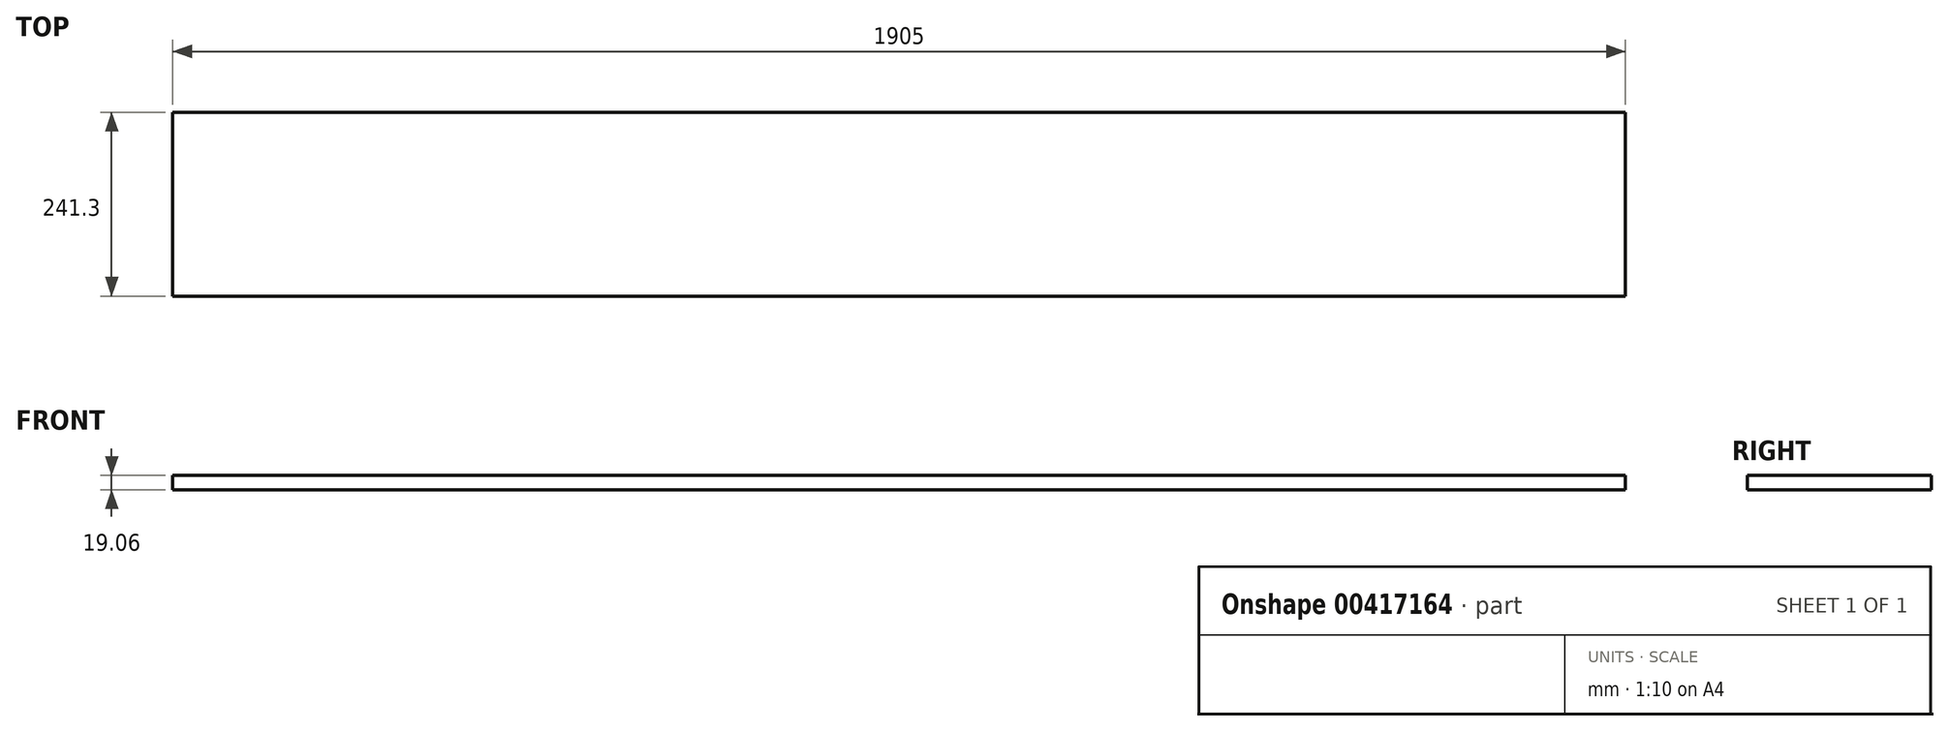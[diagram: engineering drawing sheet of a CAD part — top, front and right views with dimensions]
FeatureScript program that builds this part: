
annotation { "Feature Type Name" : "Feature", "Feature Type Description" : "" }
export const myFeature = defineFeature(function(context is Context, id is Id, definition is map)
    precondition{}
    {
        {
            var Q0;
            Q0=qCreatedBy(makeId("Front.planeOp"),FACE);
            var sketch = newSketch(context, id + "F0", { "sketchPlane" : qUnion([Q0])});
            skLineSegment(sketch, "E0.bottom", {"start": v(952.5, -9.53) * mm, "end": v(-952.5, -9.53) * mm});
            skLineSegment(sketch, "E0.top", {"start": v(952.5, 9.53) * mm, "end": v(-952.5, 9.53) * mm});
            skLineSegment(sketch, "E0.left", {"start": v(952.5, -9.53) * mm, "end": v(952.5, 9.52) * mm});
            skLineSegment(sketch, "E0.right", {"start": v(-952.5, -9.53) * mm, "end": v(-952.5, 9.52) * mm});
            skPoint(sketch, "E0.middle", {"position": v(0, 0) * mm});
            skSolve(sketch);
        }
        {
            var Q0;
            Q0 = qSketchRegion(id + "F0", true);
            extrude(context, id + "F1", {"entities" : qUnion([Q0]), "depth" : 241.3 * mm});
        }
    });
